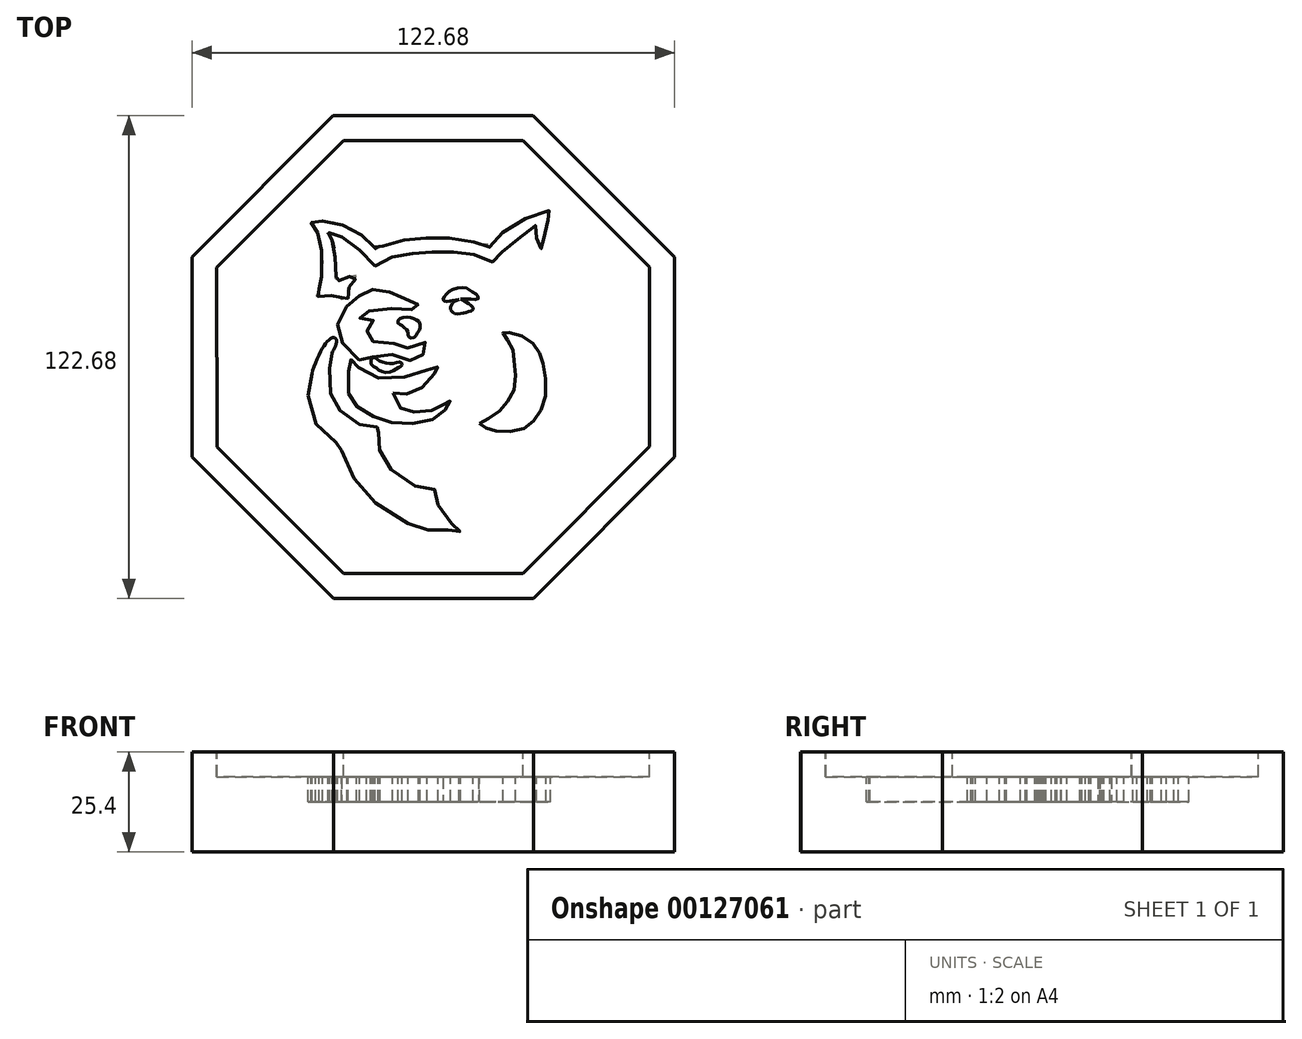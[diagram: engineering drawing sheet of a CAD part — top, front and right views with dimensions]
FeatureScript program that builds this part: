
annotation { "Feature Type Name" : "Feature", "Feature Type Description" : "" }
export const myFeature = defineFeature(function(context is Context, id is Id, definition is map)
    precondition{}
    {
        {
            var Q0;
            Q0=qCreatedBy(makeId("Top.planeOp"),FACE);
            var sketch = newSketch(context, id + "F0", { "sketchPlane" : qUnion([Q0])});
            skCircle(sketch, "E0.cCircle", {"center": v(0, 0) * mm, "radius": 61.32 * mm, "construction": true});
            skLineSegment(sketch, "E0.0", {"start": v(-61.3, -25.44) * mm, "end": v(-61.34, 25.36) * mm});
            skLineSegment(sketch, "E0.1", {"start": v(-61.34, 25.36) * mm, "end": v(-25.44, 61.3) * mm});
            skLineSegment(sketch, "E0.2", {"start": v(-25.44, 61.3) * mm, "end": v(25.36, 61.34) * mm});
            skLineSegment(sketch, "E0.3", {"start": v(25.36, 61.34) * mm, "end": v(61.3, 25.44) * mm});
            skLineSegment(sketch, "E0.4", {"start": v(61.3, 25.44) * mm, "end": v(61.34, -25.36) * mm});
            skLineSegment(sketch, "E0.5", {"start": v(61.34, -25.36) * mm, "end": v(25.44, -61.3) * mm});
            skLineSegment(sketch, "E0.6", {"start": v(25.44, -61.3) * mm, "end": v(-25.36, -61.34) * mm});
            skLineSegment(sketch, "E0.7", {"start": v(-25.36, -61.34) * mm, "end": v(-61.3, -25.44) * mm});
            skPoint(sketch, "E0.0.midPoint", {"position": v(-61.32, -0.04) * mm});
            skSolve(sketch);
        }
        {
            var Q0;
            Q0=qSketchRegion(id+"F0",true);
            extrude(context, id + "F1", {"entities" : qUnion([Q0]), "depth" : 25.4 * mm});
        }
        {
            var Q0;
            Q0=makeQuery(id+"F1.opExtrude","CAP_FACE",FACE,{"disambiguationData":[OSD([sQuery(id+"F0.wireOp",EDGE,"E0.0"),sQuery(id+"F0.wireOp",EDGE,"E0.1"),sQuery(id+"F0.wireOp",EDGE,"E0.2"),sQuery(id+"F0.wireOp",EDGE,"E0.3"),sQuery(id+"F0.wireOp",EDGE,"E0.4"),sQuery(id+"F0.wireOp",EDGE,"E0.5"),sQuery(id+"F0.wireOp",EDGE,"E0.6"),sQuery(id+"F0.wireOp",EDGE,"E0.7")])],"isStart":false});
            var sketch = newSketch(context, id + "F2", { "sketchPlane" : qUnion([Q0])});
            skLineSegment(sketch, "E1.0", {"start": v(-54.96, -22.8) * mm, "end": v(-54.99, 22.73) * mm});
            skLineSegment(sketch, "E1.1", {"start": v(-22.73, -54.99) * mm, "end": v(-54.96, -22.8) * mm});
            skLineSegment(sketch, "E1.2", {"start": v(-54.99, 22.73) * mm, "end": v(-22.8, 54.96) * mm});
            skLineSegment(sketch, "E1.3", {"start": v(22.8, -54.96) * mm, "end": v(-22.73, -54.99) * mm});
            skLineSegment(sketch, "E1.4", {"start": v(-22.8, 54.96) * mm, "end": v(22.73, 54.99) * mm});
            skLineSegment(sketch, "E1.5", {"start": v(22.73, 54.99) * mm, "end": v(54.96, 22.8) * mm});
            skLineSegment(sketch, "E1.6", {"start": v(54.96, 22.8) * mm, "end": v(54.99, -22.73) * mm});
            skLineSegment(sketch, "E1.7", {"start": v(54.99, -22.73) * mm, "end": v(22.8, -54.96) * mm});
            skSolve(sketch);
        }
        {
            var Q0;
            Q0=qSketchRegion(id+"F2",true);
            extrude(context, id + "F3", {"entities" : qUnion([Q0]), "operationType" : NewBodyOperationType.REMOVE, "oppositeDirection" : true, "depth" : 6.35 * mm});
        }
        {
            var Q0;
            Q0=makeQuery(id+"F3.boolean.opBoolean","COPY",FACE,{"derivedFrom":makeQuery(id+"F3.opExtrude","CAP_FACE",FACE,{"disambiguationData":[OSD([sQuery(id+"F2.wireOp",EDGE,"E1.0"),sQuery(id+"F2.wireOp",EDGE,"E1.1"),sQuery(id+"F2.wireOp",EDGE,"E1.2"),sQuery(id+"F2.wireOp",EDGE,"E1.3"),sQuery(id+"F2.wireOp",EDGE,"E1.4"),sQuery(id+"F2.wireOp",EDGE,"E1.5"),sQuery(id+"F2.wireOp",EDGE,"E1.6"),sQuery(id+"F2.wireOp",EDGE,"E1.7")])],"isStart":false})});
            var sketch = newSketch(context, id + "F4", { "sketchPlane" : qUnion([Q0])});
            skFitSpline(sketch, "E2", {"points": [v(4.9, 14.32) * mm, v(3.8, 14.15) * mm, v(2.86, 14.24) * mm, v(2.5, 14.68) * mm, v(3.26, 15.92) * mm, v(5, 17.16) * mm, v(8.14, 17.56) * mm, v(9.74, 16.68) * mm, v(11.2, 15.61) * mm, v(11.38, 14.81) * mm, v(9.83, 14.68) * mm, v(8.1, 14.72) * mm, v(6.19, 14.6) * mm, v(4.9, 14.32) * mm]});
            skFitSpline(sketch, "E3", {"points": [v(5.35, 14.1) * mm, v(4.73, 13.44) * mm, v(4.37, 12.28) * mm, v(4.77, 11.44) * mm, v(5.7, 11) * mm, v(7.79, 11.18) * mm, v(9.12, 11.57) * mm, v(10.14, 12.28) * mm, v(8.9, 13.62) * mm, v(7.83, 14.24) * mm, v(6.89, 14.67) * mm, v(5.35, 14.1) * mm]});
            skFitSpline(sketch, "E4", {"points": [v(-7.92, 7.94) * mm, v(-8.54, 8.25) * mm, v(-8.98, 8.7) * mm, v(-8.72, 9.62) * mm, v(-8, 9.93) * mm, v(-6.45, 10.11) * mm, v(-5.21, 9.89) * mm, v(-4.06, 9.31) * mm, v(-3.44, 8.65) * mm, v(-3.35, 7.67) * mm, v(-3.48, 6.92) * mm, v(-4.2, 5.85) * mm, v(-4.81, 5) * mm, v(-5.61, 4.83) * mm, v(-6.23, 5.14) * mm, v(-6.36, 5.67) * mm, v(-6.45, 6.56) * mm, v(-7.3, 7.4) * mm, v(-7.92, 7.94) * mm]});
            skFitSpline(sketch, "E5", {"points": [v(11.8, -16.94) * mm, v(14.9, -15.18) * mm, v(18.48, -11.8) * mm, v(20.8, -7.22) * mm, v(20.53, -0.6) * mm, v(20.03, 2.5) * mm, v(17.85, 5.74) * mm, v(17.7, 6.23) * mm, v(18.77, 6.23) * mm, v(23.84, 4.68) * mm, v(26.72, 1.44) * mm, v(28.06, -2.15) * mm, v(28.41, -10.46) * mm, v(25.95, -15.6) * mm, v(22.5, -18.35) * mm, v(16.3, -18.84) * mm, v(13.13, -17.92) * mm, v(11.8, -16.94) * mm]});
            skFitSpline(sketch, "E6", {"points": [v(-15.49, 0) * mm, v(-15.75, -1.8) * mm, v(-14.59, -2.74) * mm, v(-13.38, -3.59) * mm, v(-11.16, -3.85) * mm, v(-9.52, -3.06) * mm, v(-8.72, -2.64) * mm, v(-8.05, -2.21) * mm, v(-8, -1.63) * mm, v(-8.72, -1.21) * mm, v(-10.26, -1.63) * mm, v(-12, -1.48) * mm, v(-13.64, -1) * mm, v(-15.49, 0) * mm]});
            skFitSpline(sketch, "E7", {"points": [v(-10.26, -9.18) * mm, v(-8.57, -9.39) * mm, v(-4.72, -8.8) * mm, v(-1.77, -6.65) * mm, v(0.66, -4.06) * mm, v(1.18, -4.23) * mm, v(0.82, -1.95) * mm, v(-0.6, -2.69) * mm, v(-6.52, -4.9) * mm, v(-15.01, -5.01) * mm, v(-19.6, -1.84) * mm, v(-20.55, -0.63) * mm, v(-21.13, -0.79) * mm, v(-21.4, -1.8) * mm, v(-21.66, -7.75) * mm, v(-20.7, -11.18) * mm, v(-17.97, -13.66) * mm, v(-13.16, -15.93) * mm, v(-8.73, -16.83) * mm, v(-2.56, -16.62) * mm, v(1.34, -15.03) * mm, v(3.3, -13.19) * mm, v(4.2, -11.92) * mm, v(4.24, -11.02) * mm, v(3.61, -10.92) * mm, v(2.4, -12.18) * mm, v(0.7, -13.3) * mm, v(-3.25, -13.93) * mm, v(-6.41, -13.93) * mm, v(-8.84, -12.45) * mm, v(-10.26, -9.18) * mm]});
            skFitSpline(sketch, "E8", {"points": [v(-15.75, 9.65) * mm, v(-17.63, 9.65) * mm, v(-18.62, 9.79) * mm, v(-18.62, 10.59) * mm, v(-17.78, 11.34) * mm, v(-15.7, 11.85) * mm, v(-11.9, 12.37) * mm, v(-7.86, 12.09) * mm, v(-5.46, 12.04) * mm, v(-4.7, 11.85) * mm, v(-3.91, 12.18) * mm, v(-3.86, 13.22) * mm, v(-5.84, 14.44) * mm, v(-8.28, 15.24) * mm, v(-9.93, 15.29) * mm, v(-10.58, 15.9) * mm, v(-11.67, 16.88) * mm, v(-13.97, 17.17) * mm, v(-16.79, 17.02) * mm, v(-18.2, 16.32) * mm, v(-19.23, 14.9) * mm, v(-20.5, 13.69) * mm, v(-22.66, 12.37) * mm, v(-24.12, 9.55) * mm, v(-24.17, 6.3) * mm, v(-23.37, 3.91) * mm, v(-19.94, 0.43) * mm, v(-18.25, -0.98) * mm, v(-16.65, -0.55) * mm, v(-15.49, 0) * mm, v(-13.12, 0.43) * mm, v(-9.88, 0.53) * mm, v(-6.78, -0.6) * mm, v(-5.41, -0.93) * mm, v(-4.33, -0.79) * mm, v(-2.45, 0.8) * mm, v(-1.56, 2.69) * mm, v(-1.75, 3.72) * mm, v(-3.44, 2.92) * mm, v(-6.12, 2.31) * mm, v(-7.58, 2.55) * mm, v(-9.27, 3.35) * mm, v(-10.58, 3.44) * mm, v(-14.72, 3.72) * mm, v(-16.27, 4.66) * mm, v(-16.88, 5.8) * mm, v(-16.74, 6.83) * mm, v(-15.49, 8.38) * mm, v(-15.05, 8.9) * mm, v(-15.75, 9.65) * mm]});
            skFitSpline(sketch, "E9", {"points": [v(-14.81, 23.07) * mm, v(-11.16, 25.12) * mm, v(-6.52, 26.1) * mm, v(-2.26, 26.54) * mm, v(2.26, 26.76) * mm, v(7.79, 26.4) * mm, v(11.98, 25.56) * mm, v(15.3, 24.1) * mm, v(15.62, 24.32) * mm, v(18.41, 27.69) * mm, v(22.36, 30.53) * mm, v(26.09, 33.5) * mm, v(26.22, 33.19) * mm, v(26.18, 30) * mm, v(26.62, 28.18) * mm, v(27.46, 27.51) * mm, v(27.73, 27.87) * mm, v(27.95, 29.06) * mm, v(28.44, 32.75) * mm, v(29.68, 36.03) * mm, v(29.72, 36.65) * mm, v(29.37, 37.18) * mm, v(22.05, 34.48) * mm, v(16.55, 30.53) * mm, v(14.24, 27.87) * mm, v(13.84, 28.04) * mm, v(8.12, 29.77) * mm, v(1.87, 30.26) * mm, v(-4.04, 30.08) * mm, v(-9.23, 29.37) * mm, v(-13.57, 27.82) * mm, v(-14.5, 27.47) * mm, v(-15.08, 27.95) * mm], "startDerivative": vector(93.72, 62.3) * mm, "endDerivative": vector(-35.56, 42.42) * mm});
            skFitSpline(sketch, "E10", {"points": [v(-15.08, 27.95) * mm, v(-17.53, 30.47) * mm, v(-22.01, 33.13) * mm, v(-27.25, 34.55) * mm, v(-30.09, 34.46) * mm, v(-30.97, 34.2) * mm, v(-30.8, 33.44) * mm, v(-29.47, 31.7) * mm, v(-28.53, 28.56) * mm, v(-28.36, 20.7) * mm, v(-29.02, 18.1) * mm, v(-29.16, 16.94) * mm, v(-29.9, 15.74) * mm, v(-29.07, 15.34) * mm, v(-26.94, 15.65) * mm, v(-24.85, 15.47) * mm, v(-23.3, 15.34) * mm, v(-23.21, 14.8) * mm, v(-22.5, 14.76) * mm, v(-21.75, 14.76) * mm, v(-21.97, 16.58) * mm, v(-21.4, 17.78) * mm, v(-20.5, 19.02) * mm, v(-19.8, 19.73) * mm, v(-19.57, 20.57) * mm, v(-20.64, 20.66) * mm, v(-22.5, 20.04) * mm, v(-23.83, 19.51) * mm, v(-24.54, 19.02) * mm, v(-24.8, 19.6) * mm, v(-24.67, 21.2) * mm, v(-25.07, 26.74) * mm, v(-25.65, 29.45) * mm, v(-26.4, 30.96) * mm, v(-26.72, 31.49) * mm, v(-26.18, 31.62) * mm, v(-23.48, 30.64) * mm, v(-19, 27.47) * mm, v(-14.81, 23.07) * mm], "startDerivative": vector(-62.6, 72.42) * mm, "endDerivative": vector(86.8, -98.73) * mm});
            skFitSpline(sketch, "E11", {"points": [v(-25.78, 0.98) * mm, v(-25.15, 2.25) * mm, v(-24.51, 4.08) * mm, v(-25.15, 4.93) * mm, v(-26.63, 4.22) * mm, v(-28.53, 1.54) * mm, v(-30.85, -4.23) * mm], "startDerivative": vector(4.22, 8.66) * mm, "endDerivative": vector(-4.76, -18.24) * mm});
            skFitSpline(sketch, "E12", {"points": [v(-30.85, -4.23) * mm, v(-31.77, -8.95) * mm, v(-29.58, -17.4) * mm, v(-24.44, -21.83) * mm, v(-23.74, -21.98) * mm, v(-23.6, -22.75) * mm, v(-20.5, -30.14) * mm, v(-12.75, -38.52) * mm, v(-2.54, -43.88) * mm, v(-1, -43.95) * mm, v(3.37, -43.88) * mm, v(5.77, -44.58) * mm, v(6.68, -44.44) * mm, v(6.75, -43.6) * mm, v(5.42, -42.68) * mm, v(2.1, -39.86) * mm, v(0.7, -34.23) * mm, v(0.56, -33.74) * mm, v(-1, -33.6) * mm, v(-7.61, -31.34) * mm, v(-12.68, -25.78) * mm, v(-13.95, -22.33) * mm, v(-13.95, -19.16) * mm, v(-13.74, -18.1) * mm, v(-13.6, -17.6) * mm, v(-15, -17.96) * mm, v(-18.39, -17.33) * mm, v(-23.25, -13.88) * mm, v(-25.57, -11.41) * mm, v(-26.27, -5.07) * mm, v(-26.27, -0.92) * mm, v(-25.78, 0.98) * mm], "startDerivative": vector(-33.36, -112.8) * mm, "endDerivative": vector(24.67, 72.35) * mm});
            skSolve(sketch);
        }
        {
            var Q0;
            Q0 = qSketchRegion(id + "F4", true);
            extrude(context, id + "F5", {"entities" : qUnion([Q0]), "operationType" : NewBodyOperationType.REMOVE, "oppositeDirection" : true, "depth" : 6.35 * mm});
        }
    });
